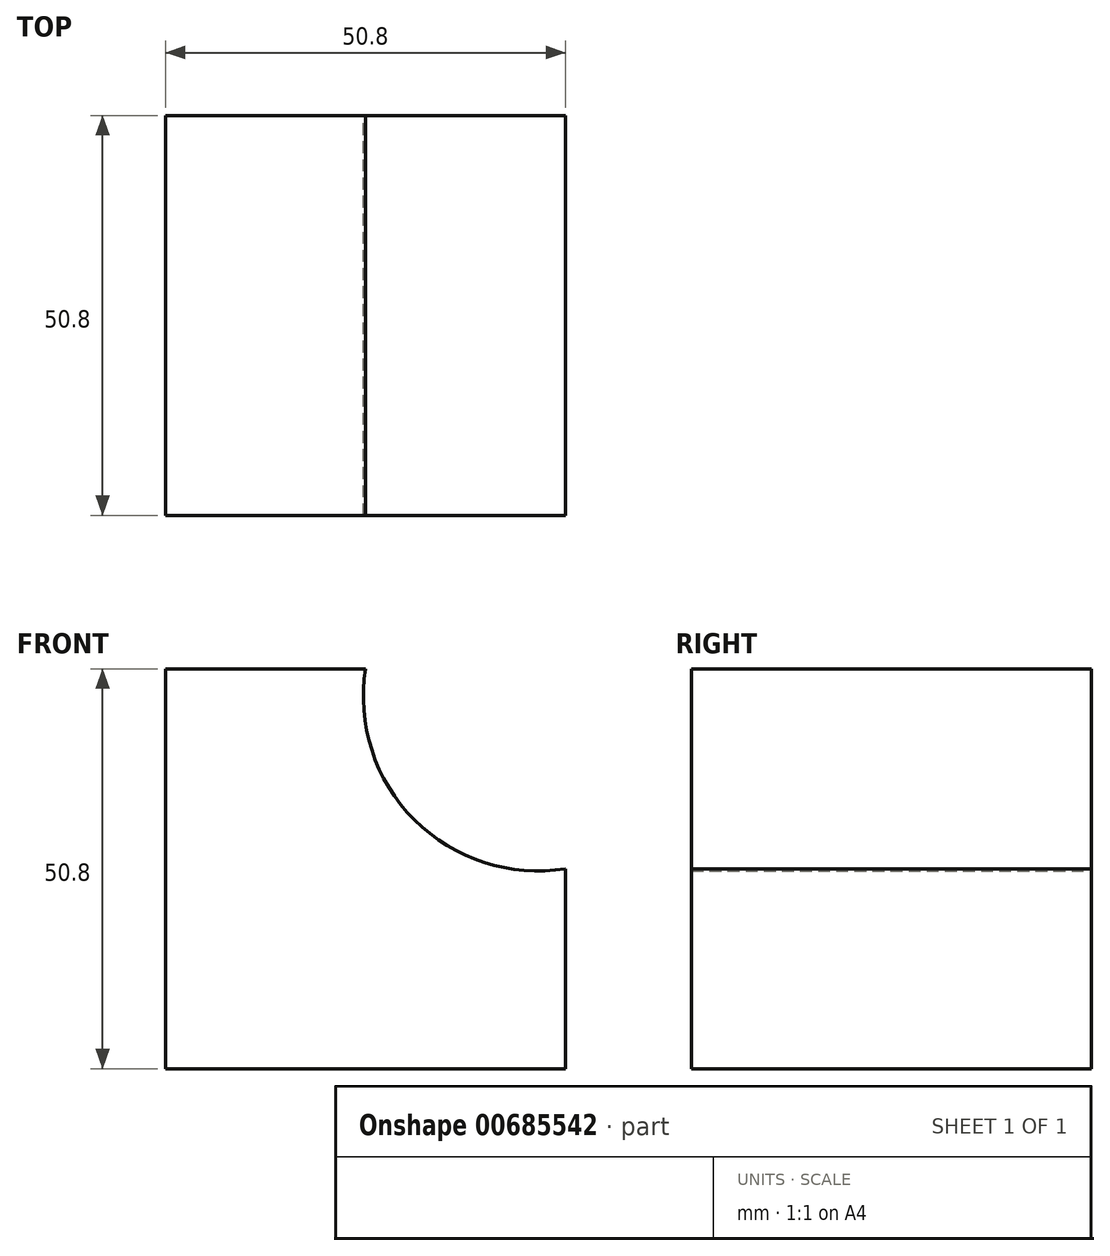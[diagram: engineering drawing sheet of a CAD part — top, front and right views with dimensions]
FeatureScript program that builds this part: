
annotation { "Feature Type Name" : "Feature", "Feature Type Description" : "" }
export const myFeature = defineFeature(function(context is Context, id is Id, definition is map)
    precondition{}
    {
        {
            var Q0;
            Q0=qCreatedBy(makeId("Front.planeOp"),FACE);
            var sketch = newSketch(context, id + "F0", { "sketchPlane" : qUnion([Q0])});
            skLineSegment(sketch, "E0", {"start": v(0, 0) * mm, "end": v(-50.8, 0) * mm});
            skLineSegment(sketch, "E1", {"start": v(-50.8, 0) * mm, "end": v(-50.8, 50.8) * mm});
            skLineSegment(sketch, "E2", {"start": v(-50.8, 50.8) * mm, "end": v(-25.4, 50.8) * mm});
            skLineSegment(sketch, "E3", {"start": v(0, 0) * mm, "end": v(0, 25.4) * mm});
            skArc(sketch, "E4", {"start": v(-25.4, 50.8) * mm, "mid": v(-19.2, 31.6) * mm, "end": v(0, 25.4) * mm});
            skSolve(sketch);
        }
        {
            var Q0;
            Q0=makeQuery(id+"F0.imprint","IMPRINT",FACE,{"disambiguationData":[TD([[makeQuery(id+"F0.imprint","IMPRINT",EDGE,{"derivedFrom":sQuery(id+"F0.wireOp",EDGE,"E0")}),-1.0]])]});
            extrude(context, id + "F1", {"entities" : qUnion([Q0]), "depth" : 50.8 * mm, "offsetDistance" : 25.4 * mm});
        }
    });
